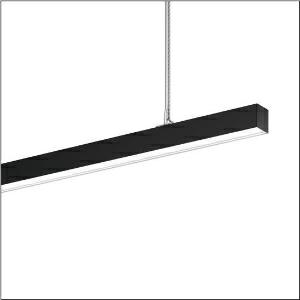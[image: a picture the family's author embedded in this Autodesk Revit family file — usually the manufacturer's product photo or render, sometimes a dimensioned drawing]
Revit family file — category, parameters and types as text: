
# Revit family: silica_r__21_51mx33da37bb_2abf
name_source: partatom
category: Lighting Fixtures
units: mm (PartAtom-declared; Revit-internal decimal feet)

## family parameters
Cut with Voids When Loaded = No
Host = Face
Light Source = No
Part Type = Normal
Room Calculation Point = No
Round Connector Dimension = Use Diameter
Shared = No

## types (1)
- --- (1 x LED, 5910 lm, 41.3 W, 3000K)
    Apparent Load = 41 VA
    CIE Flux Codes = 78 96 99 55 100
    Color Rendering = 80
    Color Temperature = 3000K
    Default Elevation = 1800 mm
    Description = Silica® 21, office luminaire, primary optical cover: prismatic diffuser, of PMMA, CAT 2 (L<= 3000cd/m²), light emission: direct/indirect distribution, primary light characteristic: symmetric, installation type: suspended mounting, LED, rated luminous flux: 5.910lm, luminous efficacy: 143lm/W, light colour: 830, colour temperature: 3000K, with terminal, 3+2-pole, max. 2.5mm², mains connection: 220..240V, AC, 50/60Hz, rated input power: 41.3W, luminaire housing, of aluminium, jet black (RAL 9005), length: 1.204mm, width: 53mm, height: 53mm, protection rating (complete): IP20, insulation class (complete): insulation class I (protective earthing), certification: CE, permissible operating ambient temperature: 0..+35°C, standard: EN 50419, packaging unit: 1 piece
    Height = 53 mm
    Lamp = 1 x LED
    Lamp Light Flux = 5910 lm
    Lamp Power = 41.3 W
    Lamp count = 1
    Length = 1204 mm
    Luminous efficacy = 143 lm/W
    Manufacturer = Siteco
    ModVariant = No
    Model = 51MX33DA37BB
    Mounting Place = Ceiling
    Mounting Type = Pendant
    Number of Poles = 1
    OnlyDefault = Yes
    Power Factor = 1
    Product Name = Silica® 21
    Product group = office luminaire | ceiling pendant
    ProductGroupID = 902
    Protection Class = Protection class I
    Protection Degree = IP 20
    RLX_Detail_Level = 1
    RLX_Emergency_Light_Flux = 0 lm
    RLX_Emergency_Type = 0
    RLX_Emergency_Type_DB = No
    RlxData = <blob elided: 26005 chars, md5=3ee6af56>
    Socket = socket
    Standby Power = 0 W
    System Light Flux = 5910 lm
    System Power = 41 W
    Type Comments = factory setting: luminous flux: 100 % | dim-lin: 254 | 345 mA
    Type Image = l_1297744.jpg
    URL = http://relux.com
    VarID = @adj_049071
    Voltage = 0 V
    Weight = 0.00 kg
    Width = 53 mm

## geometry (parser evidence)
native form markers: Blend x4, Sweep x12
no freeform markers — native parametric forms only
